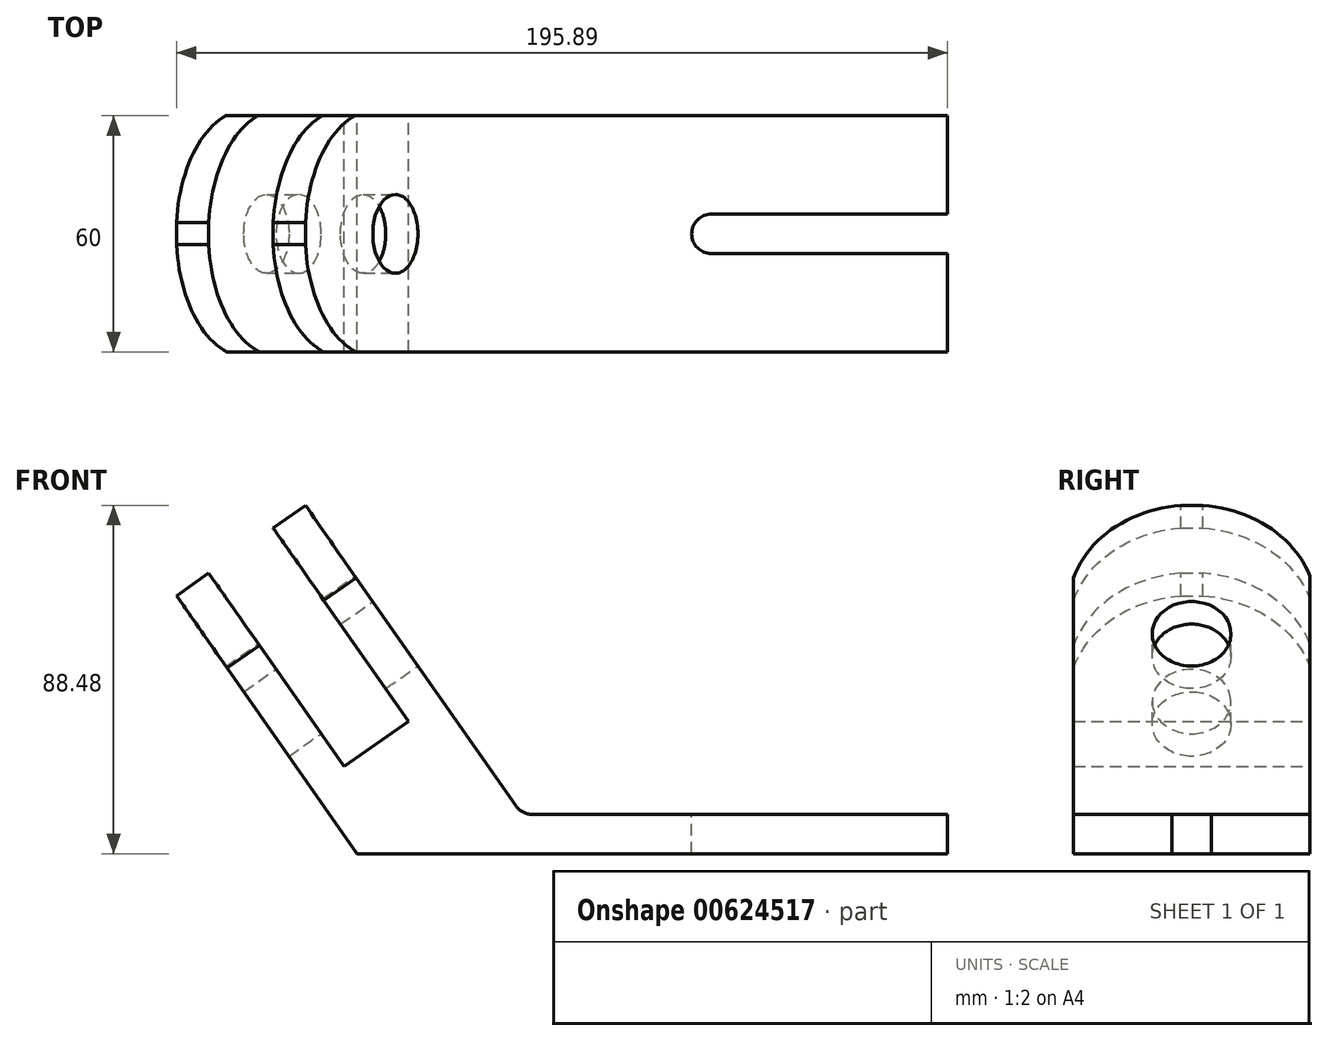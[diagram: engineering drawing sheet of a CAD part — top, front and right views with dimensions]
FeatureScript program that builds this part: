
annotation { "Feature Type Name" : "Feature", "Feature Type Description" : "" }
export const myFeature = defineFeature(function(context is Context, id is Id, definition is map)
    precondition{}
    {
        {
            var Q0;
            Q0=qCreatedBy(makeId("Front.planeOp"),FACE);
            var sketch = newSketch(context, id + "F0", { "sketchPlane" : qUnion([Q0])});
            skLineSegment(sketch, "E0", {"start": v(29.79, -34.18) * mm, "end": v(-120.21, -34.18) * mm});
            skLineSegment(sketch, "E1", {"start": v(-120.21, -34.18) * mm, "end": v(-166.1, 31.36) * mm});
            skLineSegment(sketch, "E2", {"start": v(29.79, -34.18) * mm, "end": v(29.79, -24.18) * mm});
            skLineSegment(sketch, "E3", {"start": v(-166.1, 31.36) * mm, "end": v(-157.9, 37.1) * mm});
            skLineSegment(sketch, "E4", {"start": v(-157.9, 37.1) * mm, "end": v(-123.5, -12.06) * mm});
            skLineSegment(sketch, "E5", {"start": v(-123.5, -12.06) * mm, "end": v(-107.11, -0.59) * mm});
            skLineSegment(sketch, "E6", {"start": v(-107.11, -0.59) * mm, "end": v(-141.53, 48.56) * mm});
            skLineSegment(sketch, "E7", {"start": v(-141.53, 48.56) * mm, "end": v(-133.33, 54.3) * mm});
            skLineSegment(sketch, "E8", {"start": v(-133.33, 54.3) * mm, "end": v(-98.92, 5.15) * mm});
            skLineSegment(sketch, "E9", {"start": v(-98.92, 5.15) * mm, "end": v(-78.39, -24.18) * mm});
            skLineSegment(sketch, "E10", {"start": v(-78.39, -24.18) * mm, "end": v(29.79, -24.18) * mm});
            skSolve(sketch);
        }
        {
            var Q0;
            Q0 = qSketchRegion(id + "F0", true);
            extrude(context, id + "F1", {"entities" : qUnion([Q0]), "depth" : 60 * mm, "offsetDistance" : 25 * mm});
        }
        {
            var Q0;
            Q0=makeQuery(id+"F1.opExtrude","SWEPT_FACE",FACE,{"disambiguationData":[OSD([sQuery(id+"F0.wireOp",EDGE,"E8"),sQuery(id+"F0.wireOp",EDGE,"E9")])]});
            var sketch = newSketch(context, id + "F2", { "sketchPlane" : qUnion([Q0])});
            skArc(sketch, "E11", {"start": v(0, 80.45) * mm, "mid": v(-29.66, 121.08) * mm, "end": v(-60, 80.95) * mm});
            skLineSegment(sketch, "E12", {"start": v(0, 80.45) * mm, "end": v(29.21, 131.17) * mm});
            skLineSegment(sketch, "E13", {"start": v(29.21, 131.17) * mm, "end": v(-70.87, 149.55) * mm});
            skLineSegment(sketch, "E14", {"start": v(-70.87, 149.55) * mm, "end": v(-73.54, 96.86) * mm});
            skLineSegment(sketch, "E15", {"start": v(-73.54, 96.86) * mm, "end": v(-60, 80.95) * mm});
            skSolve(sketch);
        }
        {
            var Q0;
            Q0 = qSketchRegion(id + "F2", true);
            extrude(context, id + "F3", {"entities" : qUnion([Q0]), "operationType" : NewBodyOperationType.REMOVE, "endBound" : BoundingType.THROUGH_ALL, "oppositeDirection" : true, "depth" : 25 * mm, "offsetDistance" : 25 * mm});
        }
        {
            var Q0;
            Q0=makeQuery(id+"F1.opExtrude","SWEPT_FACE",FACE,{"disambiguationData":[OSD([sQuery(id+"F0.wireOp",EDGE,"E8"),sQuery(id+"F0.wireOp",EDGE,"E9")])]});
            var sketch = newSketch(context, id + "F4", { "sketchPlane" : qUnion([Q0])});
            skCircle(sketch, "E16", {"center": v(-30, 81.16) * mm, "radius": 10 * mm});
            skPoint(sketch, "E16.centerSnap0", {"position": v(-30, 25.16) * mm});
            skSolve(sketch);
        }
        {
            var Q0;
            Q0 = qSketchRegion(id + "F4", true);
            extrude(context, id + "F5", {"entities" : qUnion([Q0]), "operationType" : NewBodyOperationType.REMOVE, "oppositeDirection" : true, "depth" : 52.1 * mm, "offsetDistance" : 25 * mm});
        }
        {
            var Q0;
            Q0=makeQuery(id+"F1.opExtrude","SWEPT_FACE",FACE,{"disambiguationData":[OSD([sQuery(id+"F0.wireOp",EDGE,"E10")])]});
            var sketch = newSketch(context, id + "F6", { "sketchPlane" : qUnion([Q0])});
            skCircle(sketch, "E17", {"center": v(-30.21, -30) * mm, "radius": 5 * mm});
            skPoint(sketch, "E17.centerSnap0", {"position": v(29.79, -30) * mm});
            skLineSegment(sketch, "E18", {"start": v(-30.21, -35) * mm, "end": v(33.63, -35) * mm});
            skLineSegment(sketch, "E19", {"start": v(-30.21, -25) * mm, "end": v(34.83, -25) * mm});
            skLineSegment(sketch, "E20", {"start": v(34.83, -25) * mm, "end": v(33.63, -35) * mm});
            skSolve(sketch);
        }
        {
            var Q0;
            Q0 = qSketchRegion(id + "F6", true);
            extrude(context, id + "F7", {"entities" : qUnion([Q0]), "operationType" : NewBodyOperationType.REMOVE, "oppositeDirection" : true, "depth" : 25 * mm, "offsetDistance" : 25 * mm});
        }
        {
            var Q0;
            Q0=makeQuery(id+"F1.opExtrude","SWEPT_EDGE",EDGE,{"disambiguationData":[OSD([sQuery(id+"F0.wireOp",EDGE,"E9"),sQuery(id+"F0.wireOp",EDGE,"E10")])]});
            fillet(context, id + "F8", {"entities" : qUnion([Q0]), "radius" : 5 * mm, "tangentPropagation" : true, "allowEdgeOverflow" : false});
        }
    });
